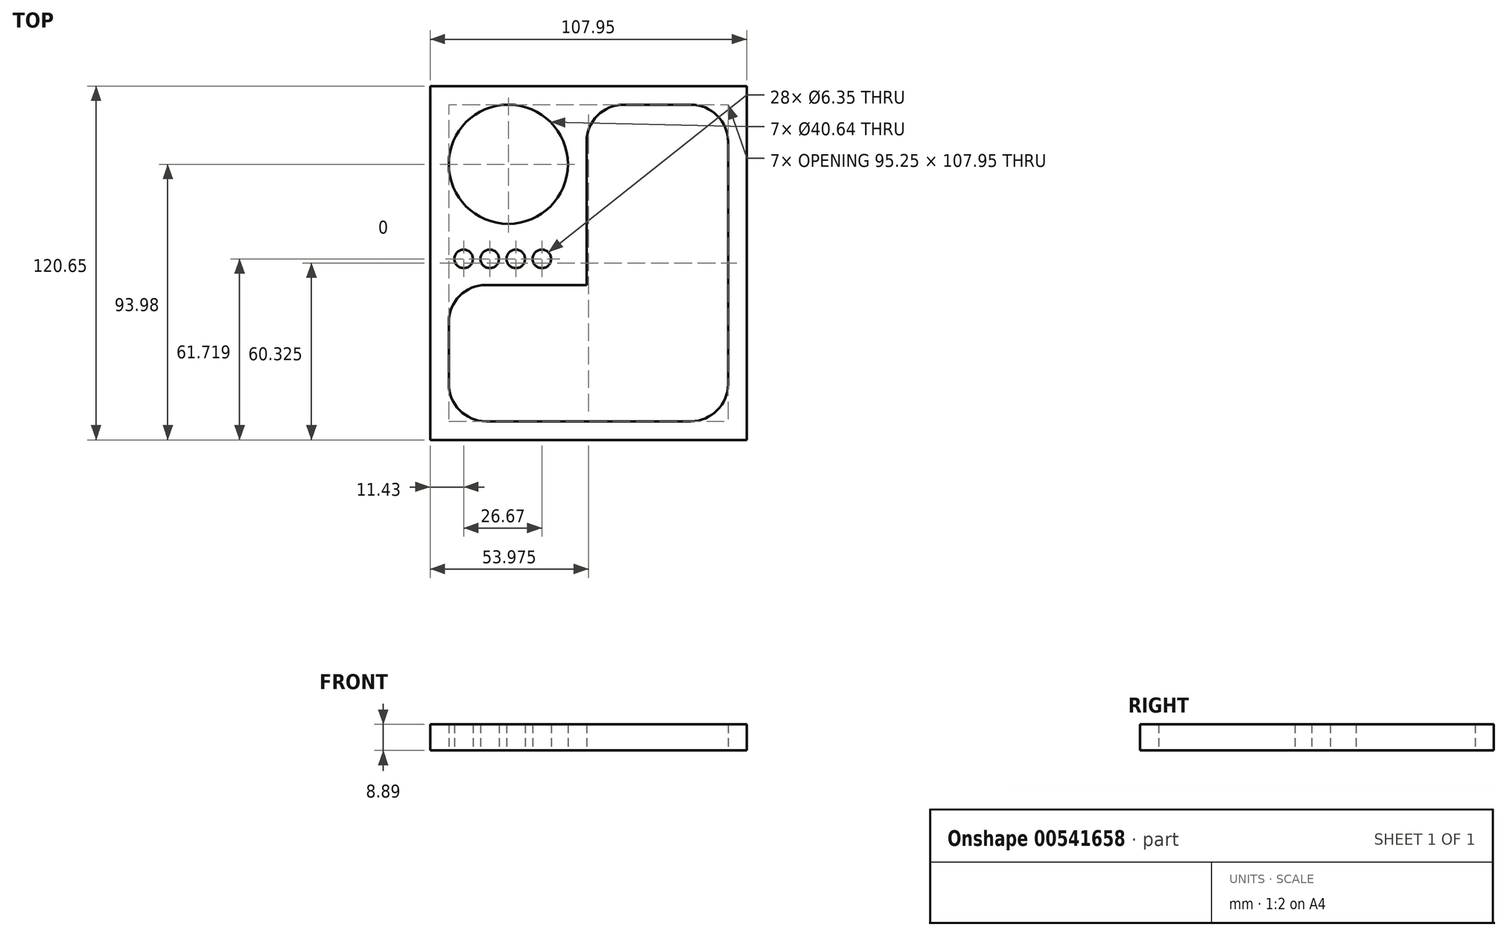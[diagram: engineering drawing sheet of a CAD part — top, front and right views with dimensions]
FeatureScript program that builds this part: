
annotation { "Feature Type Name" : "Feature", "Feature Type Description" : "" }
export const myFeature = defineFeature(function(context is Context, id is Id, definition is map)
    precondition{}
    {
        {
            var Q0;
            Q0=qCreatedBy(makeId("Top.planeOp"),FACE);
            var sketch = newSketch(context, id + "F0", { "sketchPlane" : qUnion([Q0])});
            skLineSegment(sketch, "E0.bottom", {"start": v(0, 0) * mm, "end": v(107.95, 0) * mm});
            skLineSegment(sketch, "E0.top", {"start": v(0, -120.65) * mm, "end": v(107.95, -120.65) * mm});
            skLineSegment(sketch, "E0.left", {"start": v(0, 0) * mm, "end": v(0, -120.65) * mm});
            skLineSegment(sketch, "E0.right", {"start": v(107.95, 0) * mm, "end": v(107.95, -120.65) * mm});
            skCircle(sketch, "E1", {"center": v(26.67, -26.67) * mm, "radius": 20.32 * mm});
            skLineSegment(sketch, "E2.bottom", {"start": v(66.04, -6.35) * mm, "end": v(88.9, -6.35) * mm});
            skLineSegment(sketch, "E2.top", {"start": v(53.34, -114.3) * mm, "end": v(88.9, -114.3) * mm});
            skLineSegment(sketch, "E2.left", {"start": v(53.34, -19.05) * mm, "end": v(53.34, -67.82) * mm});
            skLineSegment(sketch, "E2.right", {"start": v(101.6, -19.05) * mm, "end": v(101.6, -101.6) * mm});
            skLineSegment(sketch, "E3.bottom", {"start": v(53.34, -67.82) * mm, "end": v(19.05, -67.82) * mm});
            skLineSegment(sketch, "E3.top", {"start": v(52.83, -114.3) * mm, "end": v(19.05, -114.3) * mm});
            skLineSegment(sketch, "E3.right", {"start": v(6.35, -80.52) * mm, "end": v(6.35, -101.6) * mm});
            skPoint(sketch, "E4.visualSharp", {"position": v(53.34, -6.35) * mm});
            skArc(sketch, "E4.filletArc", {"start": v(66.04, -6.35) * mm, "mid": v(57.06, -10.07) * mm, "end": v(53.34, -19.05) * mm});
            skPoint(sketch, "E5.visualSharp", {"position": v(101.6, -6.35) * mm});
            skArc(sketch, "E5.filletArc", {"start": v(101.6, -19.05) * mm, "mid": v(97.88, -10.07) * mm, "end": v(88.9, -6.35) * mm});
            skPoint(sketch, "E6.visualSharp", {"position": v(101.6, -114.3) * mm});
            skArc(sketch, "E6.filletArc", {"start": v(88.9, -114.3) * mm, "mid": v(97.88, -110.58) * mm, "end": v(101.6, -101.6) * mm});
            skPoint(sketch, "E7.visualSharp", {"position": v(6.35, -114.3) * mm});
            skArc(sketch, "E7.filletArc", {"start": v(6.35, -101.6) * mm, "mid": v(10.07, -110.58) * mm, "end": v(19.05, -114.3) * mm});
            skPoint(sketch, "E8.visualSharp", {"position": v(6.35, -67.82) * mm});
            skArc(sketch, "E8.filletArc", {"start": v(19.05, -67.82) * mm, "mid": v(10.07, -71.54) * mm, "end": v(6.35, -80.52) * mm});
            skCircle(sketch, "E9", {"center": v(11.43, -58.93) * mm, "radius": 3.18 * mm});
            skCircle(sketch, "E10", {"center": v(20.32, -58.93) * mm, "radius": 3.18 * mm});
            skCircle(sketch, "E11", {"center": v(29.21, -58.93) * mm, "radius": 3.18 * mm});
            skCircle(sketch, "E12", {"center": v(38.1, -58.93) * mm, "radius": 3.18 * mm});
            skLineSegment(sketch, "E13", {"start": v(53.34, -114.3) * mm, "end": v(19.05, -114.3) * mm});
            skSolve(sketch);
        }
        {
            var Q0;
            Q0=makeQuery(id+"F0.imprint","IMPRINT",FACE,{"disambiguationData":[TD([[makeQuery(id+"F0.imprint","IMPRINT",EDGE,{"derivedFrom":sQuery(id+"F0.wireOp",EDGE,"E0.bottom")}),-1.0]])]});
            extrude(context, id + "F1", {"entities" : qUnion([Q0]), "depth" : 8.9 * mm, "offsetDistance" : 25.4 * mm});
        }
    });
